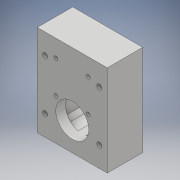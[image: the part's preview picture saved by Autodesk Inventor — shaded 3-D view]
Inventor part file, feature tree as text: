
AUTODESK INVENTOR PART (.ipt)
format: ipt  version: 2018 (Build 220112000, 112)  size: 444,928 bytes
history: native  units: mm
features: sketch x22, projected_geometry x19, extrude x18, hole x4, fillet x3, chamfer x1, mirror x1
ambient origin geometry x8: Origin, YZ Plane, XZ Plane, XY Plane, X Axis, Y Axis, Z Axis, Center Point
bodies: Solid1 (feature_tree)
feature tree (68):
  extrude  "Extrusion1"  Depth=45.0mm
  extrude  "Extrusion2"  Depth=2.25mm
  hole  "Hole1"  [1 undecoded]
  hole  "Hole2"  [1 undecoded]
  fillet  "Fillet1"  Radius=14.0mm
  extrude  "Extrusion3"  Depth=18.5mm
  extrude  "Extrusion4"  Depth=10.0mm
  extrude  "Extrusion5"  Depth=2.195mm
  extrude  "Extrusion6"  Depth=20.5mm
  hole  "Hole3"  [1 undecoded]
  extrude  "Extrusion7"  Depth=0.5mm
  extrude  "Extrusion8"  Depth=5.0mm TaperAngle=0.0deg
  extrude  "Extrusion9"  Depth=10.0mm
  extrude  "Extrusion10"  Depth=10.0mm
  extrude  "Extrusion11"  Depth=14.5mm
  extrude  "Extrusion12"  Depth=14.5mm
  extrude  "Extrusion13"  Depth=5.0mm
  extrude  "Extrusion14"  Depth=5.0mm
  extrude  "Extrusion15"  Depth=5.0mm
  extrude  "Extrusion16"  Depth=5.0mm
  extrude  "Extrusion17"  Depth=5.0mm
  chamfer  "Chamfer1"  Distance=1.0mm
  fillet  "Fillet7"  Radius=20.7mm
  fillet  "Fillet8"  Radius=32.0mm
  mirror  "Mirror1"
  extrude  "Extrusion18"  Depth=5.0mm TaperAngle=0.0deg
  hole  "Hole5"  [1 undecoded]
  sketch  "Sketch1"  dims[d0=24.5mm d1=45.0mm]
  sketch  "Sketch2"  dims[d2=1.95mm d3=0.0mm d4=2.25mm]
  projected_geometry  "Projected Loop1"
  sketch  "Sketch3"  dims[d5=20.0mm d6=2.25mm]
  projected_geometry  "Projected Loop2"
  sketch  "Sketch4"  dims[d7=5.25mm d8=5.25mm d9=14.0mm]
  projected_geometry  "Projected Loop3"
  sketch  "Sketch5"  dims[d10=5.25mm d11=18.5mm]
  projected_geometry  "Projected Loop4"
  sketch  "Sketch6"  dims[d12=10.0mm d13=0.0mm d14=20.5mm]
  projected_geometry  "Projected Loop5"
  sketch  "Sketch7"  dims[d15=2.0mm d16=2.195mm]
  projected_geometry  "Projected Loop6"
  sketch  "Sketch8"  dims[d17=2.0mm]
  projected_geometry  "Projected Loop7"
  sketch  "Sketch9"  dims[d18=2.4mm d19=6.0mm d20=4.4mm d21=2.0mm d22=90.0deg d23=8.0mm d24=20.594885mm d25=20.5mm]
  projected_geometry  "Projected Loop8"
  projected_geometry  "Projected Loop9"
  sketch  "Sketch10"  dims[d26=26.65mm d27=2.0mm]
  projected_geometry  "Projected Loop10"
  projected_geometry  "Projected Loop11"
  sketch  "Sketch11"  dims[d28=2.0mm]
  projected_geometry  "Projected Loop12"
  sketch  "Sketch12"  dims[d29=2.4mm d30=6.0mm d31=4.4mm d32=2.0mm d33=90.0deg d34=8.0mm d35=20.594885mm d36=0.5mm]
  sketch  "Sketch13"  dims[d37=18.0mm d38=5.0mm d39=0.0mm]
  sketch  "Sketch14"  dims[d41=10.0mm d42=0.0mm d43=24.5mm]
  projected_geometry  "Projected Loop13"
  sketch  "Sketch15"  dims[d44=1.15mm d45=0.0mm d46=10.0mm]
  sketch  "Sketch16"  dims[d47=21.0mm d48=14.5mm]
  projected_geometry  "Projected Loop14"
  sketch  "Sketch17"  dims[d49=20.0mm d50=14.5mm]
  projected_geometry  "Projected Loop15"
  sketch  "Sketch18"  dims[d51=24.5mm d52=5.0mm]
  projected_geometry  "Projected Loop16"
  sketch  "Sketch19"  dims[d53=5.0mm d54=2.25mm]
  projected_geometry  "Projected Loop17"
  sketch  "Sketch20"  dims[d55=2.25mm d56=5.0mm]
  projected_geometry  "Projected Loop18"
  sketch  "Sketch22"  dims[d57=5.0mm d58=9.0mm]
  sketch  "Sketch24"  dims[d59=14.75mm d60=4.0mm d61=1.0mm d62=0.0mm d63=20.7mm d64=2.4mm d65=6.0mm d66=4.4mm d67=2.0mm d68=90.0deg d69=8.0mm d70=20.594885mm d72=32.0mm d73=5.0mm d74=0.0mm d75=1.0mm d76=0.0mm d77=12.25mm d78=0.0mm d80=8.0mm d81=4.5mm d82=0.0mm d84=0.2mm d85=0.0mm d86=21.0mm d87=0.5mm d88=0.0mm d91=8.0mm d92=0.0mm d93=5.0mm d94=0.0mm d95=5.0mm d96=0.0mm d98=0.2mm d99=0.0mm d100=0.2mm d101=0.0mm d102=2.5mm d103=2.0mm d104=45.0deg d105=1.5mm d114=0.5mm d115=22.55mm d116=0.0mm d117=5.0mm d118=5.0mm d119=13.0mm d120=13.0mm d121=3.2mm d122=6.0mm d123=6.3mm d124=2.0mm d125=90.0deg d126=8.0mm d127=20.594885mm]
  projected_geometry  "Projected Loop21"
note: 4 required parameter values undecoded (feature->parameter linkage not recoverable at this tier; creation-order binding heuristic only, values carry confidence <= 0.55)
